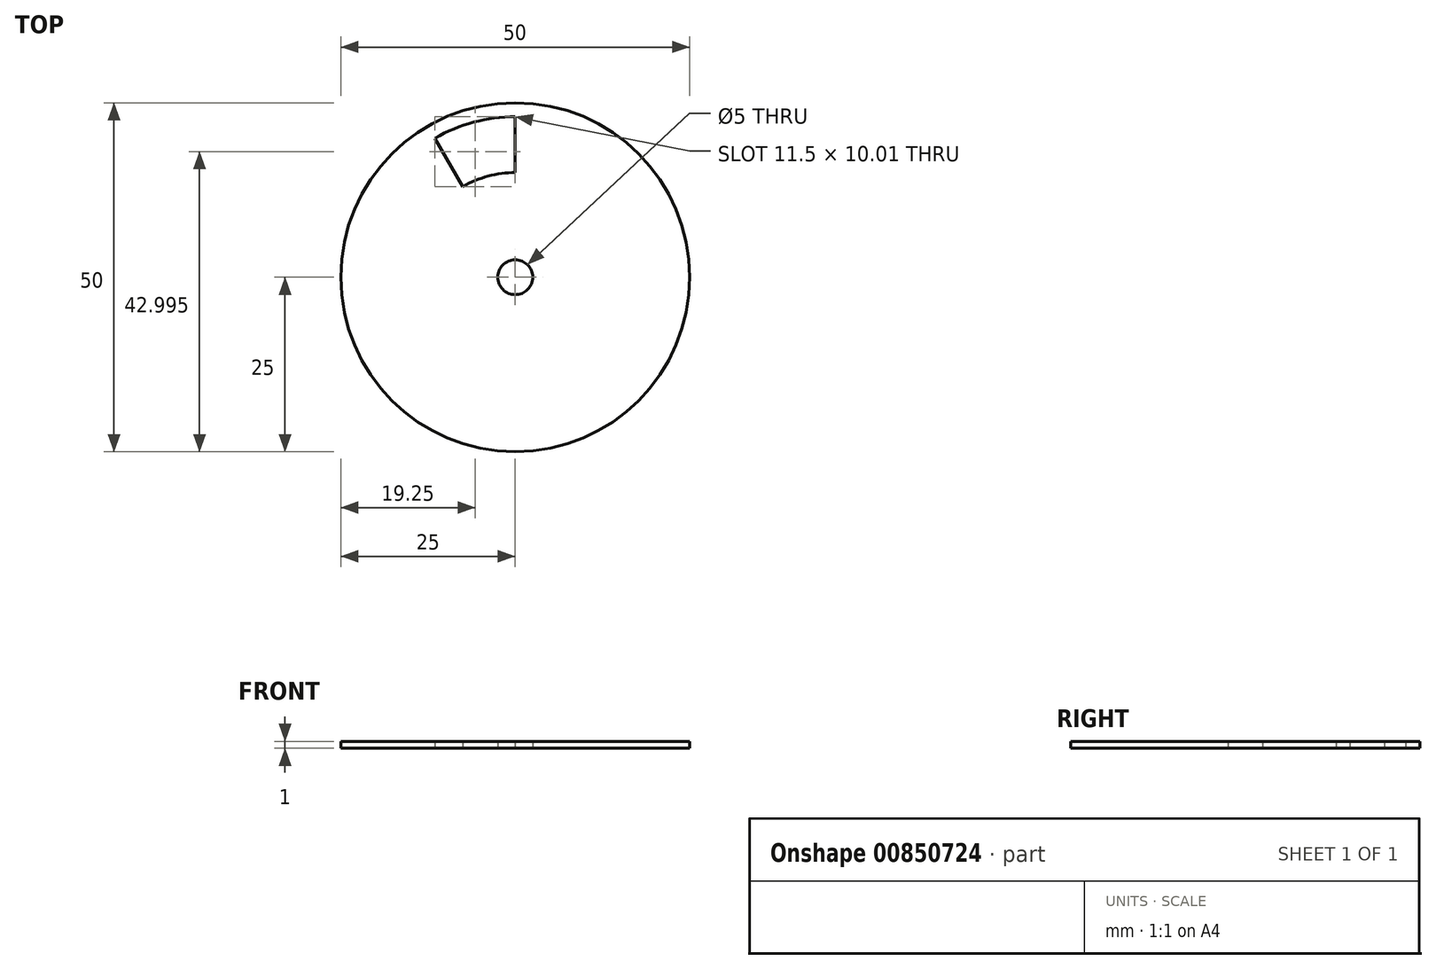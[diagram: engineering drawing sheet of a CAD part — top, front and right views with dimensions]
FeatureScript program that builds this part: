
annotation { "Feature Type Name" : "Feature", "Feature Type Description" : "" }
export const myFeature = defineFeature(function(context is Context, id is Id, definition is map)
    precondition{}
    {
        {
            var Q0;
            Q0=qCreatedBy(makeId("Top.planeOp"),FACE);
            var sketch = newSketch(context, id + "F0", { "sketchPlane" : qUnion([Q0])});
            skCircle(sketch, "E0", {"center": v(0, 0) * mm, "radius": 25 * mm});
            skCircle(sketch, "E1", {"center": v(0, 0) * mm, "radius": 2.5 * mm});
            skLineSegment(sketch, "E2", {"start": v(0, 15) * mm, "end": v(0, 23) * mm});
            skArc(sketch, "E3", {"start": v(0, 23) * mm, "mid": v(-5.95, 22.22) * mm, "end": v(-11.5, 19.92) * mm});
            skArc(sketch, "E4", {"start": v(0, 15) * mm, "mid": v(-3.88, 14.49) * mm, "end": v(-7.5, 13) * mm});
            skLineSegment(sketch, "E5", {"start": v(-7.5, 13) * mm, "end": v(-11.5, 19.92) * mm});
            skLineSegment(sketch, "E6", {"start": v(0, 0) * mm, "end": v(-11.5, 19.92) * mm, "construction": true});
            skCircle(sketch, "E7", {"center": v(0, 0) * mm, "radius": 23 * mm, "construction": true});
            skCircle(sketch, "E8", {"center": v(0, 0) * mm, "radius": 15 * mm, "construction": true});
            skLineSegment(sketch, "E9", {"start": v(0, 0) * mm, "end": v(-14.78, 17.62) * mm, "construction": true});
            skLineSegment(sketch, "E10", {"start": v(0, 0) * mm, "end": v(-23, 0) * mm});
            skSolve(sketch);
        }
        {
            var Q0;
            Q0 = qSketchRegion(id + "F0", true);
            extrude(context, id + "F1", {"entities" : qUnion([Q0]), "depth" : 1 * mm, "offsetDistance" : 25 * mm});
        }
    });
